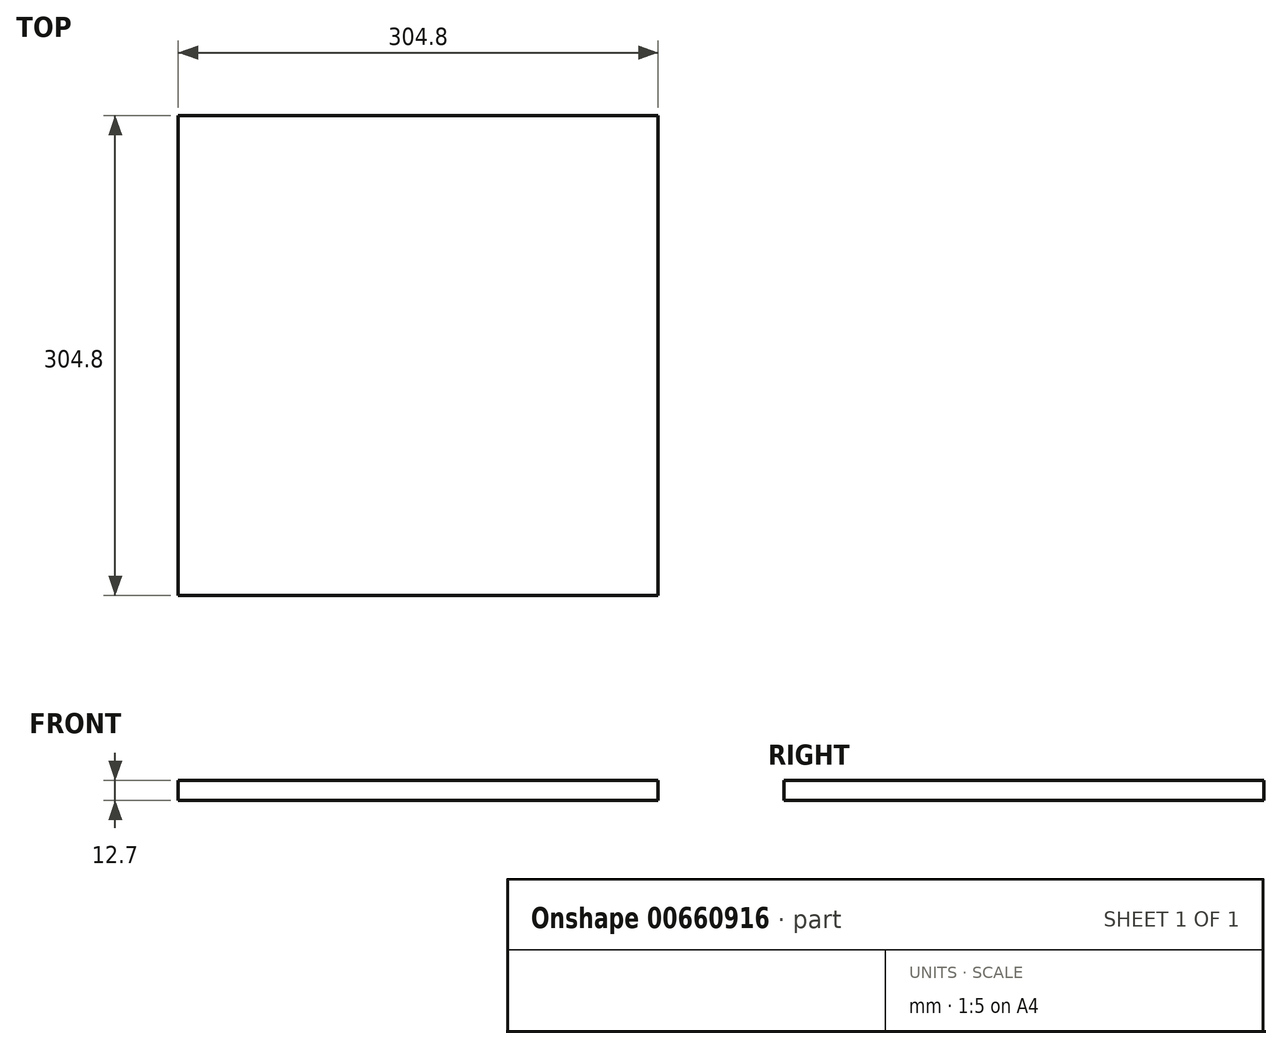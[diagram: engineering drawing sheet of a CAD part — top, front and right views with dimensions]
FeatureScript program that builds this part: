
annotation { "Feature Type Name" : "Feature", "Feature Type Description" : "" }
export const myFeature = defineFeature(function(context is Context, id is Id, definition is map)
    precondition{}
    {
        {
            var Q0;
            Q0=qCreatedBy(makeId("Front.planeOp"),FACE);
            var sketch = newSketch(context, id + "F0", { "sketchPlane" : qUnion([Q0])});
            skLineSegment(sketch, "E0.bottom", {"start": v(152.4, -6.35) * mm, "end": v(-152.4, -6.35) * mm});
            skLineSegment(sketch, "E0.top", {"start": v(152.4, 6.35) * mm, "end": v(-152.4, 6.35) * mm});
            skLineSegment(sketch, "E0.left", {"start": v(152.4, -6.35) * mm, "end": v(152.4, 6.35) * mm});
            skLineSegment(sketch, "E0.right", {"start": v(-152.4, -6.35) * mm, "end": v(-152.4, 6.35) * mm});
            skPoint(sketch, "E0.middle", {"position": v(0, 0) * mm});
            skSolve(sketch);
        }
        {
            var Q0;
            Q0=makeQuery(id+"F0.imprint","IMPRINT",FACE,{"disambiguationData":[TD([[makeQuery(id+"F0.imprint","IMPRINT",EDGE,{"derivedFrom":sQuery(id+"F0.wireOp",EDGE,"E0.bottom")}),-1.0]])]});
            extrude(context, id + "F1", {"entities" : qUnion([Q0]), "depth" : 304.8 * mm, "offsetDistance" : 25.4 * mm});
        }
    });
